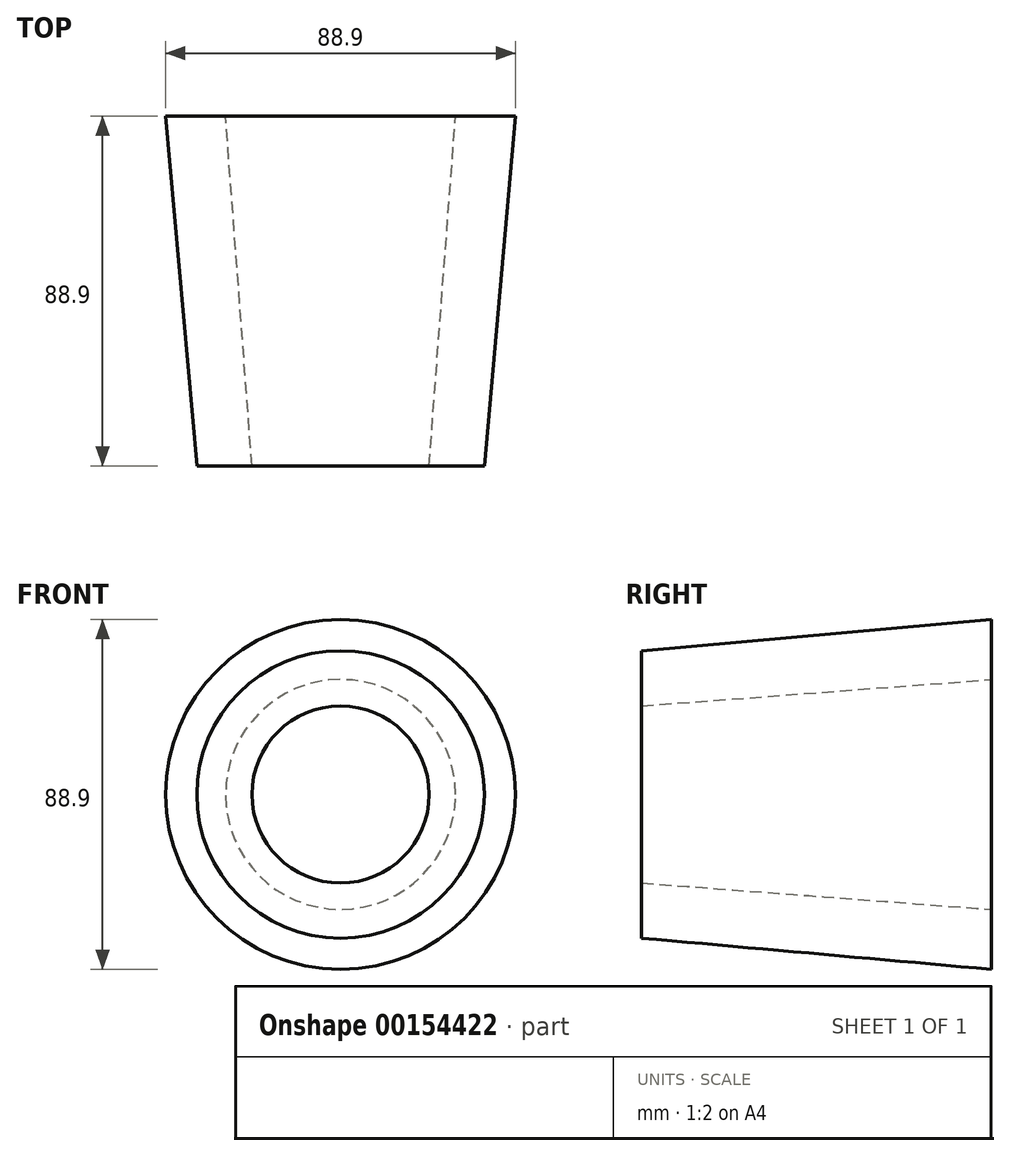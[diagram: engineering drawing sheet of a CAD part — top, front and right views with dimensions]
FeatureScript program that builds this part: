
annotation { "Feature Type Name" : "Feature", "Feature Type Description" : "" }
export const myFeature = defineFeature(function(context is Context, id is Id, definition is map)
    precondition{}
    {
        {
            var Q0;
            Q0=qCreatedBy(makeId("Front.planeOp"),FACE);
            var sketch = newSketch(context, id + "F0", { "sketchPlane" : qUnion([Q0])});
            skCircle(sketch, "E0", {"center": v(0, 0) * mm, "radius": 44.45 * mm});
            skSolve(sketch);
        }
        {
            var Q0;
            Q0=qCreatedBy(makeId("Front.planeOp"),FACE);
            cPlane(context, id + "F1", {"entities" : qUnion([Q0]), "cplaneType" : CPlaneType.OFFSET, "offset" : 88.9 * mm, "width" : 152.4 * mm, "height" : 152.4 * mm});
        }
        {
            var Q0;
            Q0=qCreatedBy(id+"F1.planeOp",FACE);
            var sketch = newSketch(context, id + "F2", { "sketchPlane" : qUnion([Q0])});
            skCircle(sketch, "E1", {"center": v(0, 0) * mm, "radius": 36.51 * mm});
            skSolve(sketch);
        }
        {
            var Q0;
            Q0=qCreatedBy(makeId("Front.planeOp"),FACE);
            var sketch = newSketch(context, id + "F3", { "sketchPlane" : qUnion([Q0])});
            skCircle(sketch, "E2.0", {"center": v(0, 0) * mm, "radius": 29.2 * mm});
            skSolve(sketch);
        }
        {
            var Q0;
            Q0=qCreatedBy(id+"F1.planeOp",FACE);
            var sketch = newSketch(context, id + "F4", { "sketchPlane" : qUnion([Q0])});
            skCircle(sketch, "E3.0", {"center": v(0, 0) * mm, "radius": 22.5 * mm});
            skSolve(sketch);
        }
        {
            var Q0;
            Q0=makeQuery(id+"F0.imprint","IMPRINT",FACE,{"disambiguationData":[TD([[makeQuery(id+"F0.imprint","IMPRINT",EDGE,{"derivedFrom":sQuery(id+"F0.wireOp",EDGE,"E0")}),1.0]])]});
            var Q1;
            Q1=makeQuery(id+"F2.imprint","IMPRINT",FACE,{"disambiguationData":[TD([[makeQuery(id+"F2.imprint","IMPRINT",EDGE,{"derivedFrom":sQuery(id+"F2.wireOp",EDGE,"E1")}),1.0]])]});
            loft(context, id + "F5", {"sheetProfilesArray" : [{ "sheetProfileEntities" : qUnion([Q0]) }, { "sheetProfileEntities" : qUnion([Q1]) }]});
        }
        {
            var Q1;
            Q1 = qSketchRegion(id + "F3", true);
            var Q2;
            Q2 = qSketchRegion(id + "F4", true);
            loft(context, id + "F6", {"operationType" : NewBodyOperationType.REMOVE, "sheetProfilesArray" : [{ "sheetProfileEntities" : qUnion([Q1]) }, { "sheetProfileEntities" : qUnion([Q2]) }]});
        }
    });
